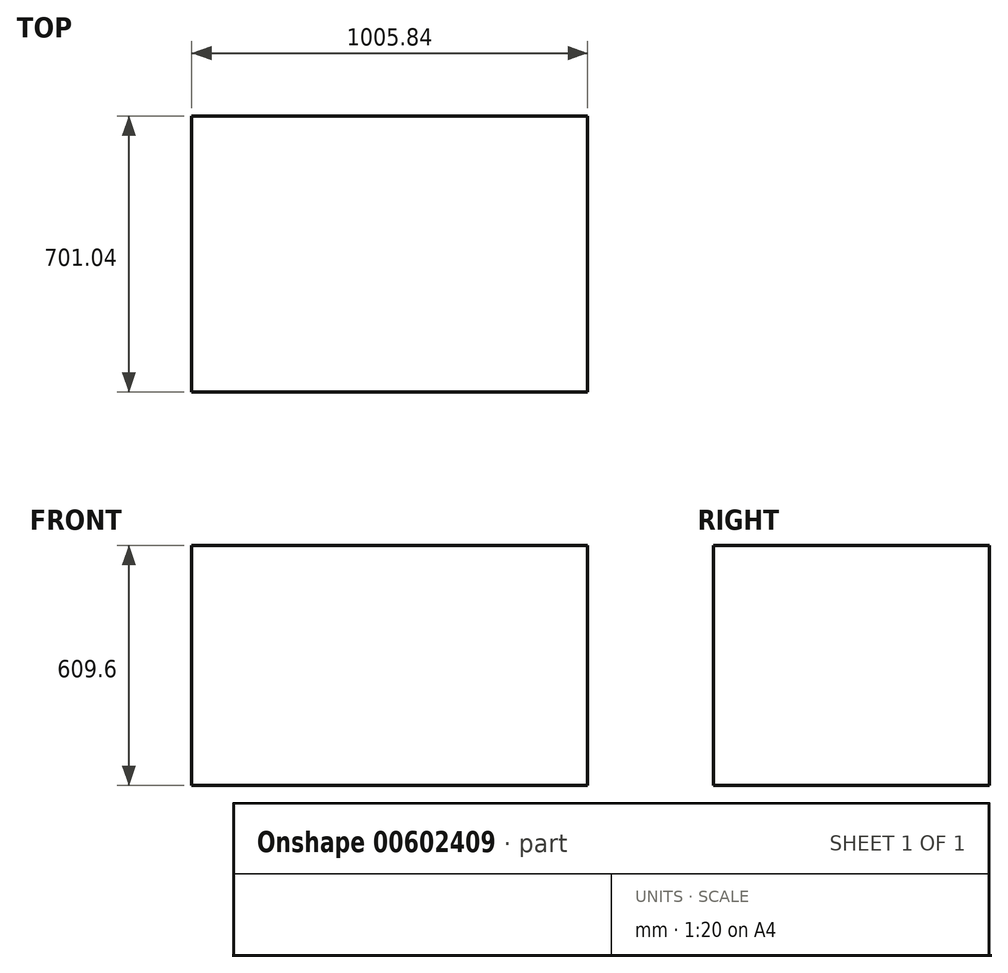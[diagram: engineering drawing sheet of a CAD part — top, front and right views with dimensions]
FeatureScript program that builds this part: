
annotation { "Feature Type Name" : "Feature", "Feature Type Description" : "" }
export const myFeature = defineFeature(function(context is Context, id is Id, definition is map)
    precondition{}
    {
        {
            var Q0;
            Q0=qCreatedBy(makeId("Top.planeOp"),FACE);
            var sketch = newSketch(context, id + "F0", { "sketchPlane" : qUnion([Q0])});
            skLineSegment(sketch, "E0.bottom", {"start": v(0, 0) * mm, "end": v(1005.84, 0) * mm});
            skLineSegment(sketch, "E0.top", {"start": v(0, -701.04) * mm, "end": v(1005.84, -701.04) * mm});
            skLineSegment(sketch, "E0.left", {"start": v(0, 0) * mm, "end": v(0, -701.04) * mm});
            skLineSegment(sketch, "E0.right", {"start": v(1005.84, 0) * mm, "end": v(1005.84, -701.04) * mm});
            skSolve(sketch);
        }
        {
            var Q0;
            Q0=makeQuery(id+"F0.imprint","IMPRINT",FACE,{"disambiguationData":[TD([[makeQuery(id+"F0.imprint","IMPRINT",EDGE,{"derivedFrom":sQuery(id+"F0.wireOp",EDGE,"E0.bottom")}),-1.0]])]});
            extrude(context, id + "F1", {"entities" : qUnion([Q0]), "depth" : 609.6 * mm, "offsetDistance" : 30.48 * mm});
        }
    });
